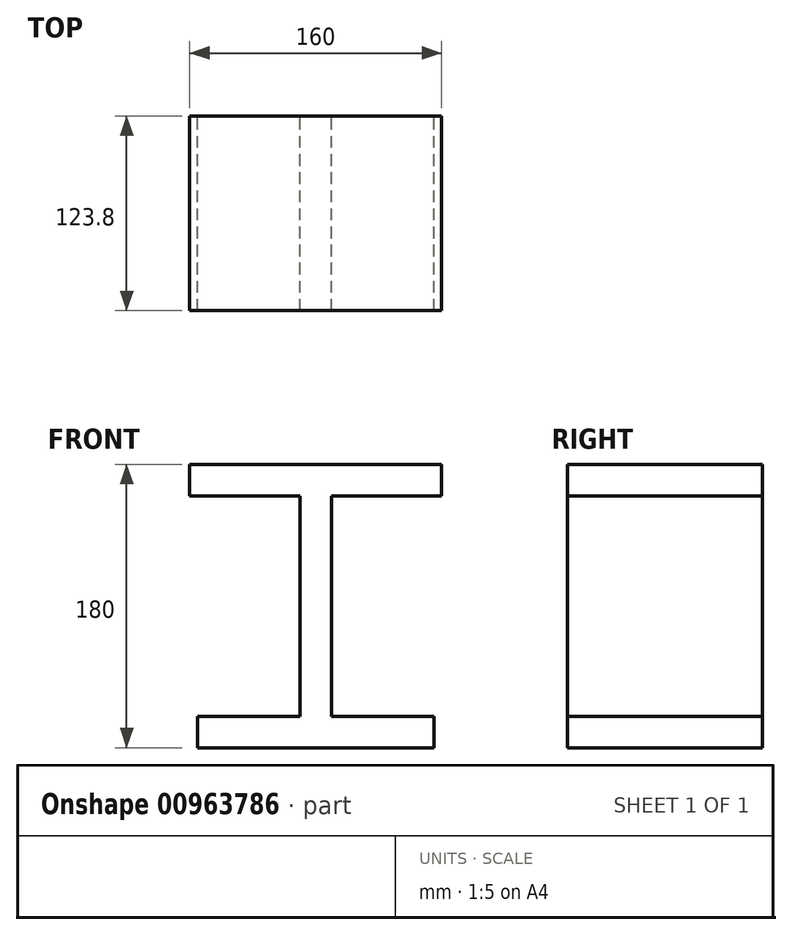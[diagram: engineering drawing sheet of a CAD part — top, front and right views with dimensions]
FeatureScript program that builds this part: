
annotation { "Feature Type Name" : "Feature", "Feature Type Description" : "" }
export const myFeature = defineFeature(function(context is Context, id is Id, definition is map)
    precondition{}
    {
        {
            var Q0;
            Q0=qCreatedBy(makeId("Front.planeOp"),FACE);
            var sketch = newSketch(context, id + "F0", { "sketchPlane" : qUnion([Q0])});
            skLineSegment(sketch, "E0.bottom", {"start": v(-80, 90) * mm, "end": v(80, 90) * mm});
            skLineSegment(sketch, "E0.top", {"start": v(-80, 70) * mm, "end": v(-10, 70) * mm});
            skLineSegment(sketch, "E0.left", {"start": v(-80, 90) * mm, "end": v(-80, 70) * mm});
            skLineSegment(sketch, "E0.right", {"start": v(80, 90) * mm, "end": v(80, 70) * mm});
            skLineSegment(sketch, "E1.bottom", {"start": v(-75, -70) * mm, "end": v(-10, -70) * mm});
            skLineSegment(sketch, "E1.top", {"start": v(-75, -90) * mm, "end": v(75, -90) * mm});
            skLineSegment(sketch, "E1.left", {"start": v(-75, -70) * mm, "end": v(-75, -90) * mm});
            skLineSegment(sketch, "E1.right", {"start": v(75, -70) * mm, "end": v(75, -90) * mm});
            skLineSegment(sketch, "E2.left", {"start": v(-10, 70) * mm, "end": v(-10, -70) * mm});
            skLineSegment(sketch, "E2.right", {"start": v(10, 70) * mm, "end": v(10, -70) * mm});
            skLineSegment(sketch, "E3.trimOffspring", {"start": v(10, 70) * mm, "end": v(80, 70) * mm});
            skLineSegment(sketch, "E4.trimOffspring", {"start": v(10, -70) * mm, "end": v(75, -70) * mm});
            skSolve(sketch);
        }
        {
            var Q0;
            Q0 = qSketchRegion(id + "F0", true);
            extrude(context, id + "F1", {"entities" : qUnion([Q0]), "depth" : 75.8 * mm, "offsetDistance" : 25 * mm});
        }
        {
            var Q0;
            Q0 = qSketchRegion(id + "F0", true);
            extrude(context, id + "F2", {"entities" : qUnion([Q0]), "operationType" : NewBodyOperationType.ADD, "endBound" : BoundingType.SYMMETRIC, "depth" : 96 * mm, "offsetDistance" : 25 * mm});
        }
    });
